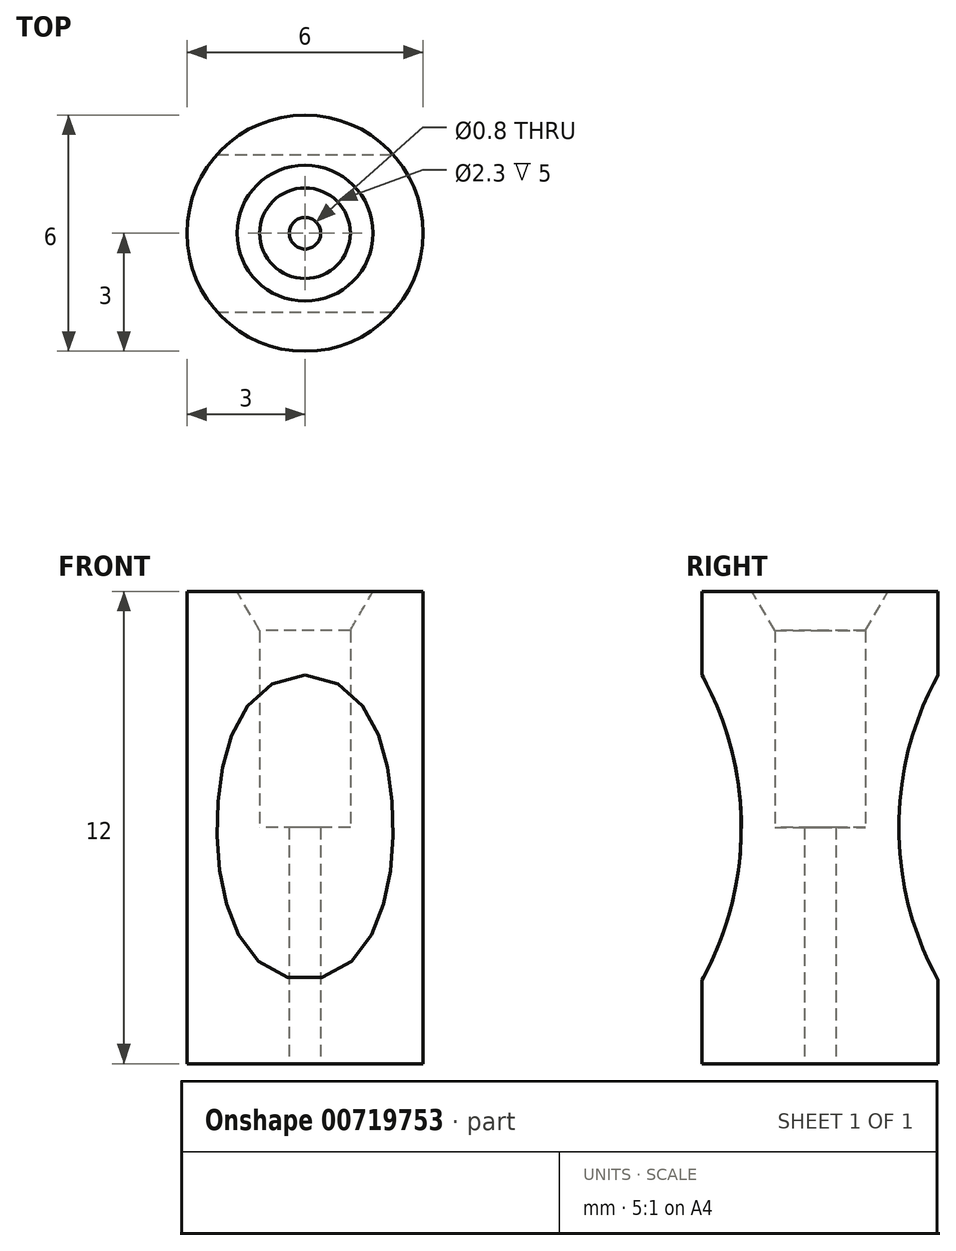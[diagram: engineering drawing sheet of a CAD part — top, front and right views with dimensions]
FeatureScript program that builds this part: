
annotation { "Feature Type Name" : "Feature", "Feature Type Description" : "" }
export const myFeature = defineFeature(function(context is Context, id is Id, definition is map)
    precondition{}
    {
        {
            var Q0;
            Q0=qCreatedBy(makeId("Top.planeOp"),FACE);
            var sketch = newSketch(context, id + "F0", { "sketchPlane" : qUnion([Q0])});
            skCircle(sketch, "E0", {"center": v(0, 0) * mm, "radius": 3 * mm});
            skCircle(sketch, "E1", {"center": v(0, 0) * mm, "radius": 0.4 * mm});
            skCircle(sketch, "E2", {"center": v(0, 0) * mm, "radius": 1.15 * mm});
            skSolve(sketch);
        }
        {
            var Q0;
            Q0=makeQuery(id+"F0.imprint","IMPRINT",FACE,{"disambiguationData":[TD([[makeQuery(id+"F0.imprint","IMPRINT",EDGE,{"derivedFrom":sQuery(id+"F0.wireOp",EDGE,"E1")}),-1.0]])]});
            extrude(context, id + "F1", {"entities" : qUnion([Q0]), "depth" : 6 * mm, "offsetDistance" : 25 * mm});
        }
        {
            var Q0;
            Q0=makeQuery(id+"F0.imprint","IMPRINT",FACE,{"disambiguationData":[TD([[makeQuery(id+"F0.imprint","IMPRINT",EDGE,{"derivedFrom":sQuery(id+"F0.wireOp",EDGE,"E0")}),1.0]])]});
            extrude(context, id + "F2", {"entities" : qUnion([Q0]), "operationType" : NewBodyOperationType.ADD, "depth" : 12 * mm, "offsetDistance" : 25 * mm});
        }
        {
            var Q0;
            Q0=makeQuery(id+"F2.opExtrude","CAP_EDGE",EDGE,{"disambiguationData":[OSD([sQuery(id+"F0.wireOp",EDGE,"E2")])],"isStart":false});
            chamfer(context, id + "F3", {"entities" : qUnion([Q0]), "chamferType" : ChamferType.OFFSET_ANGLE, "width" : 1 * mm, "oppositeDirection" : false, "angle" : 30 * degree, "tangentPropagation" : true});
        }
        {
            var Q0;
            Q0=qCreatedBy(makeId("Right.planeOp"),FACE);
            var sketch = newSketch(context, id + "F4", { "sketchPlane" : qUnion([Q0])});
            skCircle(sketch, "E3", {"center": v(10, 6) * mm, "radius": 8 * mm});
            skCircle(sketch, "E4", {"center": v(-10, 6) * mm, "radius": 8 * mm});
            skSolve(sketch);
        }
        {
            var Q0;
            Q0 = qSketchRegion(id + "F4", true);
            extrude(context, id + "F5", {"entities" : qUnion([Q0]), "operationType" : NewBodyOperationType.REMOVE, "oppositeDirection" : true, "depth" : 25 * mm, "offsetDistance" : 25 * mm, "hasSecondDirection" : true, "secondDirectionOppositeDirection" : false, "secondDirectionDepth" : 25 * mm});
        }
    });
